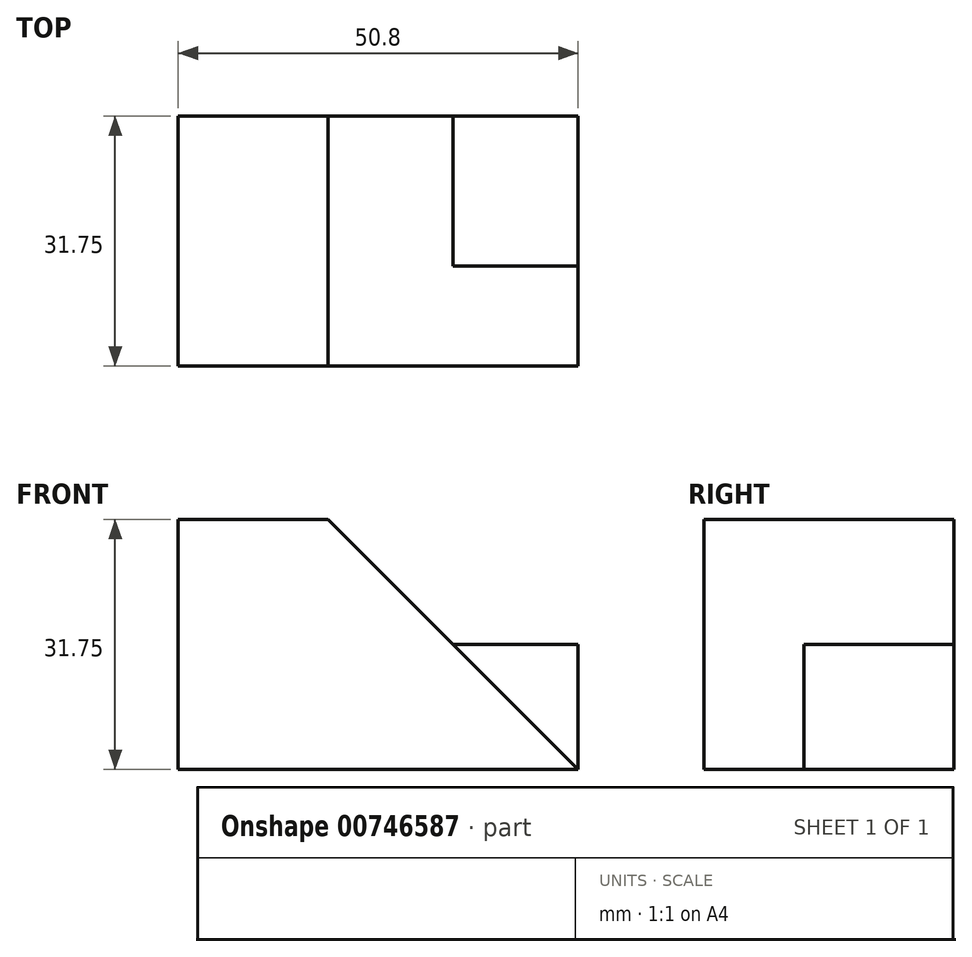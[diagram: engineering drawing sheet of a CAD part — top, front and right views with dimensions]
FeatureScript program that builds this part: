
annotation { "Feature Type Name" : "Feature", "Feature Type Description" : "" }
export const myFeature = defineFeature(function(context is Context, id is Id, definition is map)
    precondition{}
    {
        {
            var Q0;
            Q0=qCreatedBy(makeId("Front.planeOp"),FACE);
            var sketch = newSketch(context, id + "F0", { "sketchPlane" : qUnion([Q0])});
            skLineSegment(sketch, "E0", {"start": v(0, 0) * mm, "end": v(0, 31.75) * mm});
            skLineSegment(sketch, "E1", {"start": v(0, 31.75) * mm, "end": v(50.8, 31.75) * mm});
            skLineSegment(sketch, "E2", {"start": v(50.8, 31.75) * mm, "end": v(50.8, 0) * mm});
            skLineSegment(sketch, "E3", {"start": v(50.8, 0) * mm, "end": v(0, 0) * mm});
            skSolve(sketch);
        }
        {
            var Q0;
            Q0=makeQuery(id+"F0.imprint","IMPRINT",FACE,{"disambiguationData":[TD([[makeQuery(id+"F0.imprint","IMPRINT",EDGE,{"derivedFrom":sQuery(id+"F0.wireOp",EDGE,"E0")}),-1.0]])]});
            extrude(context, id + "F1", {"entities" : qUnion([Q0]), "depth" : 31.75 * mm, "offsetDistance" : 25.4 * mm});
        }
        {
            var Q0;
            Q0=makeQuery(id+"F1.opExtrude","CAP_FACE",FACE,{"disambiguationData":[OSD([sQuery(id+"F0.wireOp",EDGE,"E0"),sQuery(id+"F0.wireOp",EDGE,"E1"),sQuery(id+"F0.wireOp",EDGE,"E2"),sQuery(id+"F0.wireOp",EDGE,"E3")])],"isStart":false});
            var sketch = newSketch(context, id + "F2", { "sketchPlane" : qUnion([Q0])});
            skLineSegment(sketch, "E4", {"start": v(19.05, 31.75) * mm, "end": v(50.8, 0) * mm});
            skLineSegment(sketch, "E5", {"start": v(50.8, 0) * mm, "end": v(50.8, 31.75) * mm});
            skLineSegment(sketch, "E6", {"start": v(50.8, 31.75) * mm, "end": v(19.05, 31.75) * mm});
            skSolve(sketch);
        }
        {
            var Q0;
            Q0=makeQuery(id+"F2.imprint","IMPRINT",FACE,{"disambiguationData":[TD([[makeQuery(id+"F2.imprint","IMPRINT",EDGE,{"derivedFrom":sQuery(id+"F2.wireOp",EDGE,"E4")}),1.0]])]});
            extrude(context, id + "F3", {"entities" : qUnion([Q0]), "operationType" : NewBodyOperationType.REMOVE, "oppositeDirection" : true, "depth" : 12.7 * mm, "offsetDistance" : 25.4 * mm});
        }
        {
            var Q0;
            Q0=makeQuery(id+"F3.boolean.opBoolean","COPY",FACE,{"derivedFrom":makeQuery(id+"F3.opExtrude","CAP_FACE",FACE,{"disambiguationData":[OSD([sQuery(id+"F2.wireOp",EDGE,"E4"),sQuery(id+"F2.wireOp",EDGE,"E5"),sQuery(id+"F2.wireOp",EDGE,"E6")])],"isStart":false})});
            var sketch = newSketch(context, id + "F4", { "sketchPlane" : qUnion([Q0])});
            skLineSegment(sketch, "E7", {"start": v(34.93, 15.87) * mm, "end": v(31.75, 31.75) * mm});
            skLineSegment(sketch, "E8", {"start": v(31.75, 31.75) * mm, "end": v(19.05, 31.75) * mm});
            skLineSegment(sketch, "E9", {"start": v(19.65, 31.18) * mm, "end": v(34.93, 15.87) * mm});
            skSolve(sketch);
        }
        {
            var Q0;
            {var subQ0=sQuery(id+"F4.wireOp",EDGE,"E7");Q0=makeQuery(id+"F4.imprint","IMPRINT",FACE,{"disambiguationData":[TD([[makeQuery(id+"F4.imprint","IMPRINT",EDGE,{"derivedFrom":subQ0}),1.0]])]});}
            extrude(context, id + "F5", {"entities" : qUnion([Q0]), "operationType" : NewBodyOperationType.REMOVE, "oppositeDirection" : true, "depth" : 25.4 * mm, "offsetDistance" : 25.4 * mm});
        }
        {
            var Q0;
            Q0=makeQuery(id+"F3.boolean.opBoolean","COPY",FACE,{"derivedFrom":makeQuery(id+"F3.opExtrude","CAP_FACE",FACE,{"disambiguationData":[OSD([sQuery(id+"F2.wireOp",EDGE,"E4"),sQuery(id+"F2.wireOp",EDGE,"E5"),sQuery(id+"F2.wireOp",EDGE,"E6")])],"isStart":false})});
            var sketch = newSketch(context, id + "F6", { "sketchPlane" : qUnion([Q0])});
            skLineSegment(sketch, "E10", {"start": v(34.93, 15.87) * mm, "end": v(50.8, 15.87) * mm});
            skLineSegment(sketch, "E11", {"start": v(50.8, 15.87) * mm, "end": v(50.8, 31.75) * mm});
            skLineSegment(sketch, "E12", {"start": v(31.75, 31.75) * mm, "end": v(50.8, 31.75) * mm});
            skLineSegment(sketch, "E13", {"start": v(31.75, 31.75) * mm, "end": v(34.93, 15.87) * mm});
            skSolve(sketch);
        }
        {
            var Q0;
            Q0=makeQuery(id+"F6.imprint","IMPRINT",FACE,{"disambiguationData":[TD([[makeQuery(id+"F6.imprint","IMPRINT",EDGE,{"derivedFrom":sQuery(id+"F6.wireOp",EDGE,"E10")}),1.0]])]});
            extrude(context, id + "F7", {"entities" : qUnion([Q0]), "operationType" : NewBodyOperationType.REMOVE, "oppositeDirection" : true, "depth" : 25.4 * mm, "offsetDistance" : 25.4 * mm});
        }
    });
